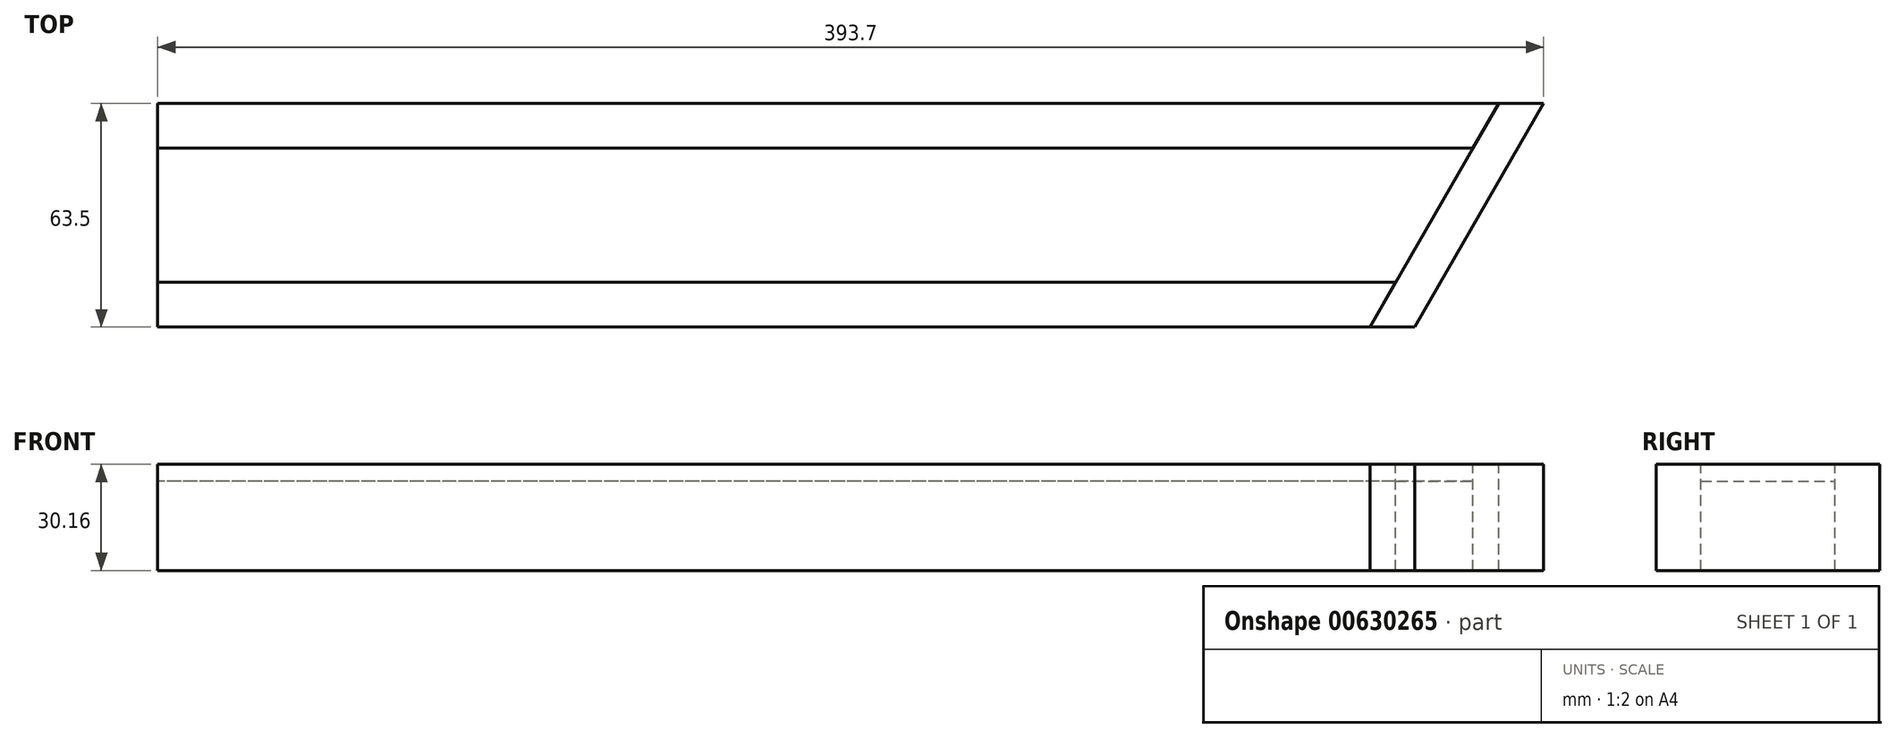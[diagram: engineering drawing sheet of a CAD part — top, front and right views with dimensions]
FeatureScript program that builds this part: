
annotation { "Feature Type Name" : "Feature", "Feature Type Description" : "" }
export const myFeature = defineFeature(function(context is Context, id is Id, definition is map)
    precondition{}
    {
        {
            var Q0;
            Q0=qCreatedBy(makeId("Right.planeOp"),FACE);
            var sketch = newSketch(context, id + "F0", { "sketchPlane" : qUnion([Q0])});
            skLineSegment(sketch, "E0.bottom", {"start": v(0, 0) * mm, "end": v(12.7, 0) * mm});
            skLineSegment(sketch, "E0.top", {"start": v(0, 30.16) * mm, "end": v(12.7, 30.16) * mm});
            skLineSegment(sketch, "E0.left", {"start": v(0, 0) * mm, "end": v(0, 30.16) * mm});
            skLineSegment(sketch, "E0.right", {"start": v(12.7, 0) * mm, "end": v(12.7, 30.16) * mm});
            skLineSegment(sketch, "E1.bottom", {"start": v(12.7, 0) * mm, "end": v(50.8, 0) * mm});
            skLineSegment(sketch, "E1.top", {"start": v(12.7, 25.4) * mm, "end": v(50.8, 25.4) * mm});
            skLineSegment(sketch, "E1.left", {"start": v(12.7, 0) * mm, "end": v(12.7, 25.4) * mm});
            skLineSegment(sketch, "E1.right", {"start": v(50.8, 0) * mm, "end": v(50.8, 25.4) * mm});
            skLineSegment(sketch, "E2.bottom", {"start": v(50.8, 0) * mm, "end": v(63.5, 0) * mm});
            skLineSegment(sketch, "E2.top", {"start": v(50.8, 30.16) * mm, "end": v(63.5, 30.16) * mm});
            skLineSegment(sketch, "E2.left", {"start": v(50.8, 0) * mm, "end": v(50.8, 30.16) * mm});
            skLineSegment(sketch, "E2.right", {"start": v(63.5, 0) * mm, "end": v(63.5, 30.16) * mm});
            skSolve(sketch);
        }
        {
            var Q0;
            Q0=makeQuery(id+"F0.imprint","IMPRINT",FACE,{"disambiguationData":[TD([[makeQuery(id+"F0.imprint","IMPRINT",EDGE,{"derivedFrom":sQuery(id+"F0.wireOp",EDGE,"E0.bottom")}),1.0]])]});
            var Q1;
            {var subQ3=sQuery(id+"F0.wireOp",EDGE,"E2.bottom");Q1=makeQuery(id+"F0.imprint","IMPRINT",FACE,{"disambiguationData":[TD([[makeQuery(id+"F0.imprint","IMPRINT",EDGE,{"derivedFrom":subQ3}),1.0]])]});}
            extrude(context, id + "F1", {"entities" : qUnion([Q0, Q1]), "depth" : 406.4 * mm, "offsetDistance" : 25.4 * mm});
        }
        {
            var Q0;
            {var subQ0=sQuery(id+"F0.wireOp",EDGE,"E1.bottom");Q0=makeQuery(id+"F0.imprint","IMPRINT",FACE,{"disambiguationData":[TD([[makeQuery(id+"F0.imprint","IMPRINT",EDGE,{"derivedFrom":subQ0}),1.0]])]});}
            var Q1;
            Q1=makeQuery(id+"F1.opExtrude","CAP_FACE",FACE,{"disambiguationData":[OSD([sQuery(id+"F0.wireOp",EDGE,"E0.bottom"),sQuery(id+"F0.wireOp",EDGE,"E0.top"),sQuery(id+"F0.wireOp",EDGE,"E0.left"),sQuery(id+"F0.wireOp",EDGE,"E0.right"),sQuery(id+"F0.wireOp",EDGE,"E1.left")])],"isStart":false});
            extrude(context, id + "F2", {"entities" : qUnion([Q0]), "endBound" : BoundingType.UP_TO_SURFACE, "depth" : 25.4 * mm, "endBoundEntityFace" : qUnion([Q1]), "offsetDistance" : 25.4 * mm});
        }
        {
            var Q0;
            Q0=makeQuery(id+"F1.opExtrude","SWEPT_FACE",FACE,{"disambiguationData":[OSD([sQuery(id+"F0.wireOp",EDGE,"E2.top")])]});
            var sketch = newSketch(context, id + "F3", { "sketchPlane" : qUnion([Q0])});
            skLineSegment(sketch, "E3", {"start": v(406.4, 63.5) * mm, "end": v(406.4, 0) * mm});
            skLineSegment(sketch, "E4", {"start": v(406.4, 0) * mm, "end": v(344.34, 0) * mm});
            skLineSegment(sketch, "E5", {"start": v(344.34, 0) * mm, "end": v(381, 63.5) * mm});
            skLineSegment(sketch, "E6", {"start": v(381, 63.5) * mm, "end": v(406.4, 63.5) * mm});
            skSolve(sketch);
        }
        {
            var Q0;
            Q0=qSketchRegion(id+"F3",true);
            extrude(context, id + "F4", {"entities" : qUnion([Q0]), "operationType" : NewBodyOperationType.REMOVE, "endBound" : BoundingType.THROUGH_ALL, "oppositeDirection" : true, "depth" : 25.4 * mm, "offsetDistance" : 25.4 * mm});
        }
        {
            var Q0;
            Q0=qCreatedBy(makeId("Top.planeOp"),FACE);
            var sketch = newSketch(context, id + "F5", { "sketchPlane" : qUnion([Q0])});
            skLineSegment(sketch, "E7", {"start": v(381, 63.5) * mm, "end": v(393.7, 63.5) * mm});
            skLineSegment(sketch, "E8", {"start": v(393.7, 63.5) * mm, "end": v(357.04, 0) * mm});
            skLineSegment(sketch, "E9", {"start": v(357.04, 0) * mm, "end": v(344.34, 0) * mm});
            skLineSegment(sketch, "E10", {"start": v(344.34, 0) * mm, "end": v(381, 63.5) * mm});
            skSolve(sketch);
        }
        {
            var Q0;
            Q0=qSketchRegion(id+"F5",true);
            var Q1;
            Q1=makeQuery(id+"F1.opExtrude","SWEPT_FACE",FACE,{"disambiguationData":[OSD([sQuery(id+"F0.wireOp",EDGE,"E2.top")])]});
            extrude(context, id + "F6", {"entities" : qUnion([Q0]), "endBound" : BoundingType.UP_TO_SURFACE, "depth" : 25.4 * mm, "endBoundEntityFace" : qUnion([Q1]), "offsetDistance" : 25.4 * mm});
        }
    });
